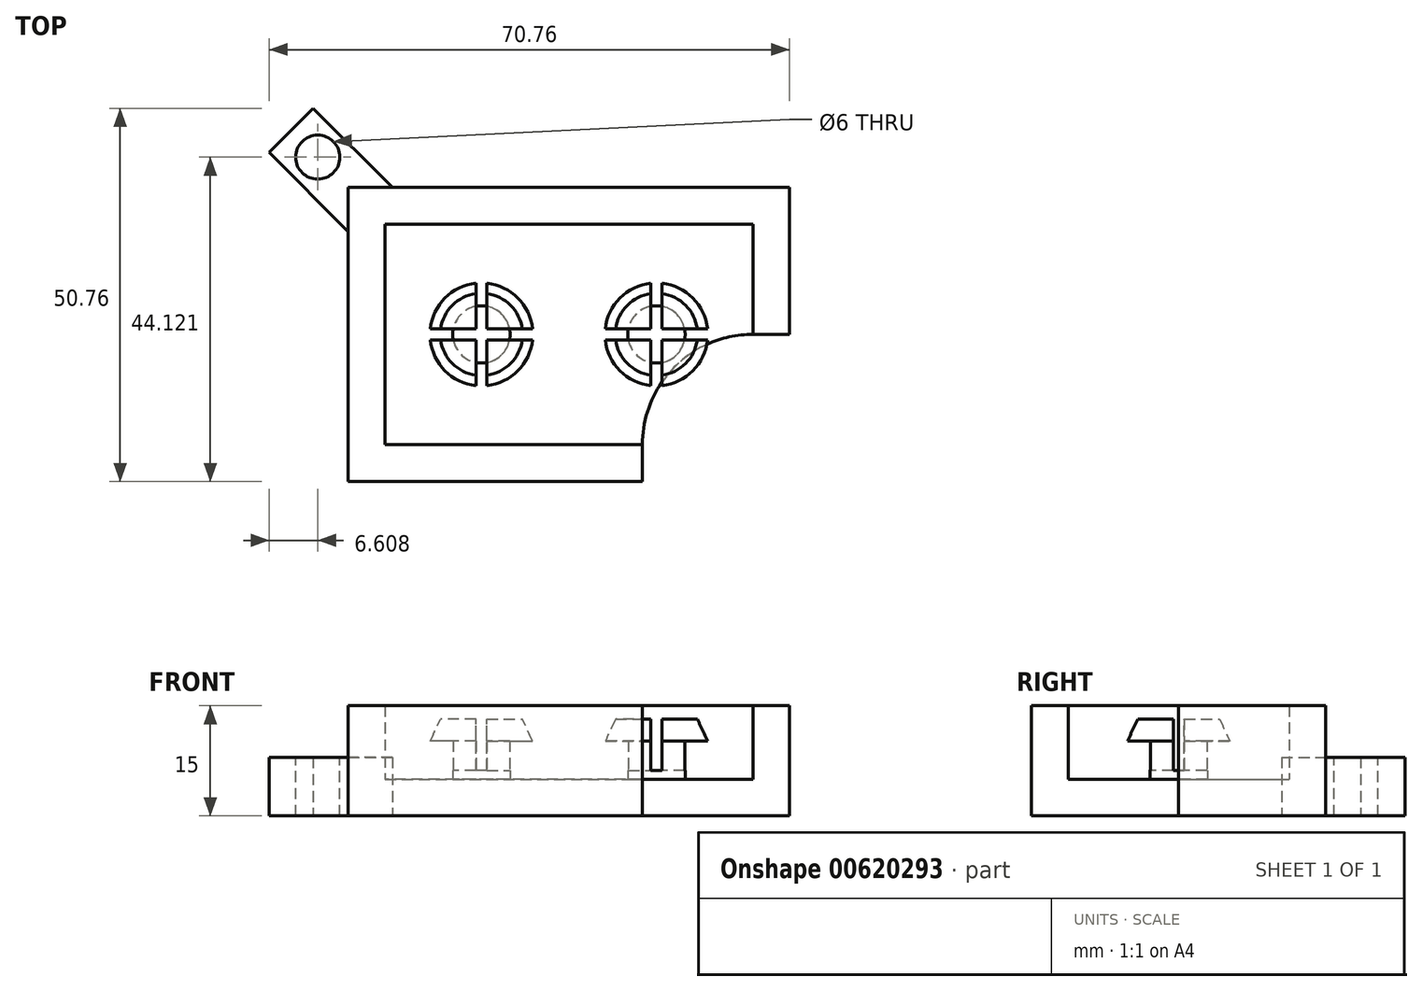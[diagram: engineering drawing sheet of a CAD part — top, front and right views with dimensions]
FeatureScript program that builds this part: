
annotation { "Feature Type Name" : "Feature", "Feature Type Description" : "" }
export const myFeature = defineFeature(function(context is Context, id is Id, definition is map)
    precondition{}
    {
        {
            var Q0;
            Q0=qCreatedBy(makeId("Top.planeOp"),FACE);
            var sketch = newSketch(context, id + "F0", { "sketchPlane" : qUnion([Q0])});
            skLineSegment(sketch, "E0.bottom", {"start": v(30, 20) * mm, "end": v(-30, 20) * mm});
            skLineSegment(sketch, "E0.top", {"start": v(30, -20) * mm, "end": v(-30, -20) * mm});
            skLineSegment(sketch, "E0.left", {"start": v(30, 20) * mm, "end": v(30, -20) * mm});
            skLineSegment(sketch, "E0.right", {"start": v(-30, 20) * mm, "end": v(-30, -20) * mm});
            skPoint(sketch, "E0.middle", {"position": v(0, 0) * mm});
            skSolve(sketch);
        }
        {
            var Q0;
            Q0=qSketchRegion(id+"F0",true);
            extrude(context, id + "F1", {"entities" : qUnion([Q0]), "depth" : 5 * mm, "offsetDistance" : 25 * mm});
        }
        {
            var Q0;
            Q0=makeQuery(id+"F1.opExtrude","CAP_FACE",FACE,{"disambiguationData":[OSD([sQuery(id+"F0.wireOp",EDGE,"E0.bottom"),sQuery(id+"F0.wireOp",EDGE,"E0.top"),sQuery(id+"F0.wireOp",EDGE,"E0.left"),sQuery(id+"F0.wireOp",EDGE,"E0.right")])],"isStart":false});
            var sketch = newSketch(context, id + "F2", { "sketchPlane" : qUnion([Q0])});
            skLineSegment(sketch, "E1.bottom", {"start": v(-30, 20) * mm, "end": v(30, 20) * mm});
            skLineSegment(sketch, "E1.top", {"start": v(-30, 15) * mm, "end": v(30, 15) * mm});
            skLineSegment(sketch, "E1.left", {"start": v(-30, 20) * mm, "end": v(-30, 15) * mm});
            skLineSegment(sketch, "E1.right", {"start": v(30, 20) * mm, "end": v(30, 15) * mm});
            skLineSegment(sketch, "E2.bottom", {"start": v(30, -20) * mm, "end": v(25, -20) * mm});
            skLineSegment(sketch, "E2.top", {"start": v(30, 15) * mm, "end": v(25, 15) * mm});
            skLineSegment(sketch, "E2.left", {"start": v(30, -20) * mm, "end": v(30, 15) * mm});
            skLineSegment(sketch, "E2.right", {"start": v(25, -20) * mm, "end": v(25, 15) * mm});
            skLineSegment(sketch, "E3.bottom", {"start": v(25, -20) * mm, "end": v(-30, -20) * mm});
            skLineSegment(sketch, "E3.top", {"start": v(25, -15) * mm, "end": v(-30, -15) * mm});
            skLineSegment(sketch, "E3.left", {"start": v(25, -20) * mm, "end": v(25, -15) * mm});
            skLineSegment(sketch, "E3.right", {"start": v(-30, -20) * mm, "end": v(-30, -15) * mm});
            skLineSegment(sketch, "E4.bottom", {"start": v(-30, -15) * mm, "end": v(-25, -15) * mm});
            skLineSegment(sketch, "E4.top", {"start": v(-30, 15) * mm, "end": v(-25, 15) * mm});
            skLineSegment(sketch, "E4.left", {"start": v(-30, -15) * mm, "end": v(-30, 15) * mm});
            skLineSegment(sketch, "E4.right", {"start": v(-25, -15) * mm, "end": v(-25, 15) * mm});
            skSolve(sketch);
        }
        {
            var Q0;
            Q0=qSketchRegion(id+"F2",true);
            extrude(context, id + "F3", {"entities" : qUnion([Q0]), "operationType" : NewBodyOperationType.ADD, "depth" : 10 * mm, "offsetDistance" : 25 * mm});
        }
        {
            var Q0;
            Q0=makeQuery(id+"F1.opExtrude","CAP_FACE",FACE,{"disambiguationData":[OSD([sQuery(id+"F0.wireOp",EDGE,"E0.bottom"),sQuery(id+"F0.wireOp",EDGE,"E0.top"),sQuery(id+"F0.wireOp",EDGE,"E0.left"),sQuery(id+"F0.wireOp",EDGE,"E0.right")])],"isStart":true});
            var sketch = newSketch(context, id + "F4", { "sketchPlane" : qUnion([Q0])});
            skLineSegment(sketch, "E5", {"start": v(30, 0) * mm, "end": v(25, 0) * mm});
            skPoint(sketch, "E5.endSnap0", {"position": v(30, 0) * mm});
            skLineSegment(sketch, "E6", {"start": v(10, 20) * mm, "end": v(10, 15) * mm});
            skArc(sketch, "E7", {"start": v(10, 15) * mm, "mid": v(14.4, 4.4) * mm, "end": v(25, 0) * mm});
            skLineSegment(sketch, "E8", {"start": v(30, 0) * mm, "end": v(30, 20) * mm});
            skLineSegment(sketch, "E9", {"start": v(30, 20) * mm, "end": v(10, 20) * mm});
            skSolve(sketch);
        }
        {
            var Q0;
            Q0=qSketchRegion(id+"F4",true);
            extrude(context, id + "F5", {"entities" : qUnion([Q0]), "operationType" : NewBodyOperationType.REMOVE, "oppositeDirection" : true, "depth" : 25 * mm, "offsetDistance" : 25 * mm});
        }
        {
            var Q0;
            Q0=makeQuery(id+"F1.opExtrude","CAP_FACE",FACE,{"disambiguationData":[OSD([sQuery(id+"F0.wireOp",EDGE,"E0.bottom"),sQuery(id+"F0.wireOp",EDGE,"E0.top"),sQuery(id+"F0.wireOp",EDGE,"E0.left"),sQuery(id+"F0.wireOp",EDGE,"E0.right")])],"isStart":false});
            var sketch = newSketch(context, id + "F6", { "sketchPlane" : qUnion([Q0])});
            skCircle(sketch, "E10.MirrorC", {"center": v(11.9, 0) * mm, "radius": 3.9 * mm});
            skCircle(sketch, "E11.MirrorC", {"center": v(-11.9, 0) * mm, "radius": 3.9 * mm});
            skSolve(sketch);
        }
        {
            var Q0;
            Q0=qSketchRegion(id+"F6",true);
            extrude(context, id + "F7", {"entities" : qUnion([Q0]), "operationType" : NewBodyOperationType.ADD, "depth" : 5.2 * mm, "offsetDistance" : 25 * mm});
        }
        {
            var Q0;
            Q0=makeQuery(id+"F7.opExtrude","CAP_FACE",FACE,{"disambiguationData":[OSD([sQuery(id+"F6.wireOp",EDGE,"E11.MirrorC")])],"isStart":false});
            var sketch = newSketch(context, id + "F8", { "sketchPlane" : qUnion([Q0])});
            skCircle(sketch, "E12", {"center": v(-11.9, 0) * mm, "radius": 7 * mm});
            skCircle(sketch, "E13.MirrorC", {"center": v(11.9, 0) * mm, "radius": 7 * mm});
            skSolve(sketch);
        }
        {
            var Q0;
            Q0 = qSketchRegion(id + "F8", true);
            extrude(context, id + "F9", {"entities" : qUnion([Q0]), "operationType" : NewBodyOperationType.ADD, "depth" : 3 * mm, "offsetDistance" : 25 * mm, "hasDraft" : true, "draftAngle" : 25 * degree, "draftPullDirection" : true});
        }
        {
            var Q0;
            Q0=makeQuery(id+"F9.opExtrude","CAP_FACE",FACE,{"disambiguationData":[OSD([sQuery(id+"F8.wireOp",EDGE,"E12")])],"isStart":false});
            var sketch = newSketch(context, id + "F10", { "sketchPlane" : qUnion([Q0])});
            skLineSegment(sketch, "E14", {"start": v(-11.9, 0) * mm, "end": v(-11.9, 7.56) * mm, "construction": true});
            skLineSegment(sketch, "E15", {"start": v(-11.9, 7.56) * mm, "end": v(-11.9, -8.43) * mm, "construction": true});
            skLineSegment(sketch, "E16", {"start": v(-19.8, 0) * mm, "end": v(-2.85, 0) * mm, "construction": true});
            skLineSegment(sketch, "E17", {"start": v(-11.9, 7.56) * mm, "end": v(-11.15, 7.56) * mm});
            skLineSegment(sketch, "E18", {"start": v(-11.15, 7.56) * mm, "end": v(-11.15, -8.43) * mm});
            skLineSegment(sketch, "E19", {"start": v(-11.15, -8.43) * mm, "end": v(-12.65, -8.43) * mm});
            skLineSegment(sketch, "E20", {"start": v(-12.65, -8.43) * mm, "end": v(-12.65, 7.56) * mm});
            skLineSegment(sketch, "E21", {"start": v(-12.65, 7.56) * mm, "end": v(-11.9, 7.56) * mm});
            skLineSegment(sketch, "E22", {"start": v(-2.85, 0) * mm, "end": v(-2.85, 0.75) * mm});
            skLineSegment(sketch, "E23", {"start": v(-2.85, 0.75) * mm, "end": v(-19.8, 0.75) * mm});
            skLineSegment(sketch, "E24", {"start": v(-19.8, 0.75) * mm, "end": v(-19.8, -0.75) * mm});
            skLineSegment(sketch, "E25", {"start": v(-19.8, -0.75) * mm, "end": v(-2.85, -0.75) * mm});
            skLineSegment(sketch, "E26", {"start": v(-2.85, -0.75) * mm, "end": v(-2.85, 0) * mm});
            skLineSegment(sketch, "E27.MirrorCS", {"start": v(12.65, 7.56) * mm, "end": v(11.9, 7.56) * mm});
            skLineSegment(sketch, "E28.MirrorCS", {"start": v(11.9, 7.56) * mm, "end": v(11.15, 7.56) * mm});
            skLineSegment(sketch, "E29.MirrorCS", {"start": v(11.15, 7.56) * mm, "end": v(11.15, -8.43) * mm});
            skLineSegment(sketch, "E30.MirrorCS", {"start": v(12.65, -8.43) * mm, "end": v(12.65, 7.56) * mm});
            skLineSegment(sketch, "E31.MirrorCS", {"start": v(2.85, 0.75) * mm, "end": v(19.8, 0.75) * mm});
            skLineSegment(sketch, "E32.MirrorCS", {"start": v(19.8, -0.75) * mm, "end": v(2.85, -0.75) * mm});
            skLineSegment(sketch, "E33.MirrorCS", {"start": v(2.85, -0.75) * mm, "end": v(2.85, 0) * mm});
            skLineSegment(sketch, "E34.MirrorCS", {"start": v(2.85, 0) * mm, "end": v(2.85, 0.75) * mm});
            skLineSegment(sketch, "E35.MirrorCS", {"start": v(19.8, 0.75) * mm, "end": v(19.8, -0.75) * mm});
            skLineSegment(sketch, "E36.MirrorCS", {"start": v(11.15, -8.43) * mm, "end": v(12.65, -8.43) * mm});
            skSolve(sketch);
        }
        {
            var Q0;
            Q0 = qSketchRegion(id + "F10", true);
            extrude(context, id + "F11", {"entities" : qUnion([Q0]), "operationType" : NewBodyOperationType.REMOVE, "oppositeDirection" : true, "depth" : 7 * mm, "offsetDistance" : 25 * mm});
        }
        {
            var Q0;
            Q0 = qSketchRegion(id + "F10", true);
            extrude(context, id + "F12", {"entities" : qUnion([Q0]), "operationType" : NewBodyOperationType.REMOVE, "oppositeDirection" : true, "depth" : 7 * mm, "offsetDistance" : 25 * mm});
        }
        {
            var Q0;
            Q0=makeQuery(id+"F1.opExtrude","CAP_FACE",FACE,{"disambiguationData":[OSD([sQuery(id+"F0.wireOp",EDGE,"E0.bottom"),sQuery(id+"F0.wireOp",EDGE,"E0.top"),sQuery(id+"F0.wireOp",EDGE,"E0.left"),sQuery(id+"F0.wireOp",EDGE,"E0.right")])],"isStart":true});
            var sketch = newSketch(context, id + "F13", { "sketchPlane" : qUnion([Q0])});
            skLineSegment(sketch, "E37", {"start": v(-29.5, -13.5) * mm, "end": v(-23.5, -19.5) * mm});
            skLineSegment(sketch, "E38", {"start": v(-23.5, -19.5) * mm, "end": v(-31.23, -27.23) * mm});
            skLineSegment(sketch, "E39", {"start": v(-31.23, -27.23) * mm, "end": v(-37.23, -21.23) * mm});
            skLineSegment(sketch, "E40", {"start": v(-37.23, -21.23) * mm, "end": v(-29.5, -13.5) * mm});
            skLineSegment(sketch, "E41", {"start": v(-37.23, -21.23) * mm, "end": v(-40.76, -24.76) * mm});
            skLineSegment(sketch, "E42", {"start": v(-31.23, -27.23) * mm, "end": v(-34.76, -30.76) * mm});
            skLineSegment(sketch, "E43", {"start": v(-40.76, -24.76) * mm, "end": v(-34.76, -30.76) * mm});
            skSolve(sketch);
        }
        {
            var Q0;
            Q0 = qSketchRegion(id + "F13", true);
            extrude(context, id + "F14", {"entities" : qUnion([Q0]), "operationType" : NewBodyOperationType.ADD, "oppositeDirection" : true, "depth" : 8 * mm, "offsetDistance" : 25 * mm});
        }
        {
            var Q0;
            Q0=makeQuery(id+"F14.opExtrude","CAP_FACE",FACE,{"disambiguationData":[OSD([sQuery(id+"F13.wireOp",EDGE,"E37"),sQuery(id+"F13.wireOp",EDGE,"E38"),sQuery(id+"F13.wireOp",EDGE,"E39"),sQuery(id+"F13.wireOp",EDGE,"E40")])],"isStart":false});
            var sketch = newSketch(context, id + "F15", { "sketchPlane" : qUnion([Q0])});
            skLineSegment(sketch, "E44", {"start": v(-34.75, 24.72) * mm, "end": v(-30, 20) * mm, "construction": true});
            skLineSegment(sketch, "E45", {"start": v(-30, 20) * mm, "end": v(-33, 17) * mm, "construction": true});
            skLineSegment(sketch, "E46", {"start": v(-33, 17) * mm, "end": v(-31.73, 27.73) * mm, "construction": true});
            skLineSegment(sketch, "E47", {"start": v(-31.73, 27.73) * mm, "end": v(-37.73, 21.73) * mm, "construction": true});
            skPoint(sketch, "E48.endSnap0", {"position": v(-32.38, 22.36) * mm});
            skLineSegment(sketch, "E49", {"start": v(-30, 20) * mm, "end": v(-27, 23) * mm, "construction": true});
            skLineSegment(sketch, "E50", {"start": v(-27, 23) * mm, "end": v(-37.73, 21.73) * mm, "construction": true});
            skCircle(sketch, "E51", {"center": v(-32.38, 22.36) * mm, "radius": 2.5 * mm, "construction": true});
            skCircle(sketch, "E52", {"center": v(-34.15, 24.12) * mm, "radius": 3 * mm});
            skSolve(sketch);
        }
        {
            var Q0;
            Q0=makeQuery(id+"F15.imprint","IMPRINT",FACE,{"disambiguationData":[TD([[makeQuery(id+"F15.imprint","IMPRINT",EDGE,{"derivedFrom":sQuery(id+"F15.wireOp",EDGE,"E52")}),1.0]])]});
            extrude(context, id + "F16", {"entities" : qUnion([Q0]), "operationType" : NewBodyOperationType.REMOVE, "oppositeDirection" : true, "depth" : 25 * mm, "offsetDistance" : 25 * mm});
        }
    });
